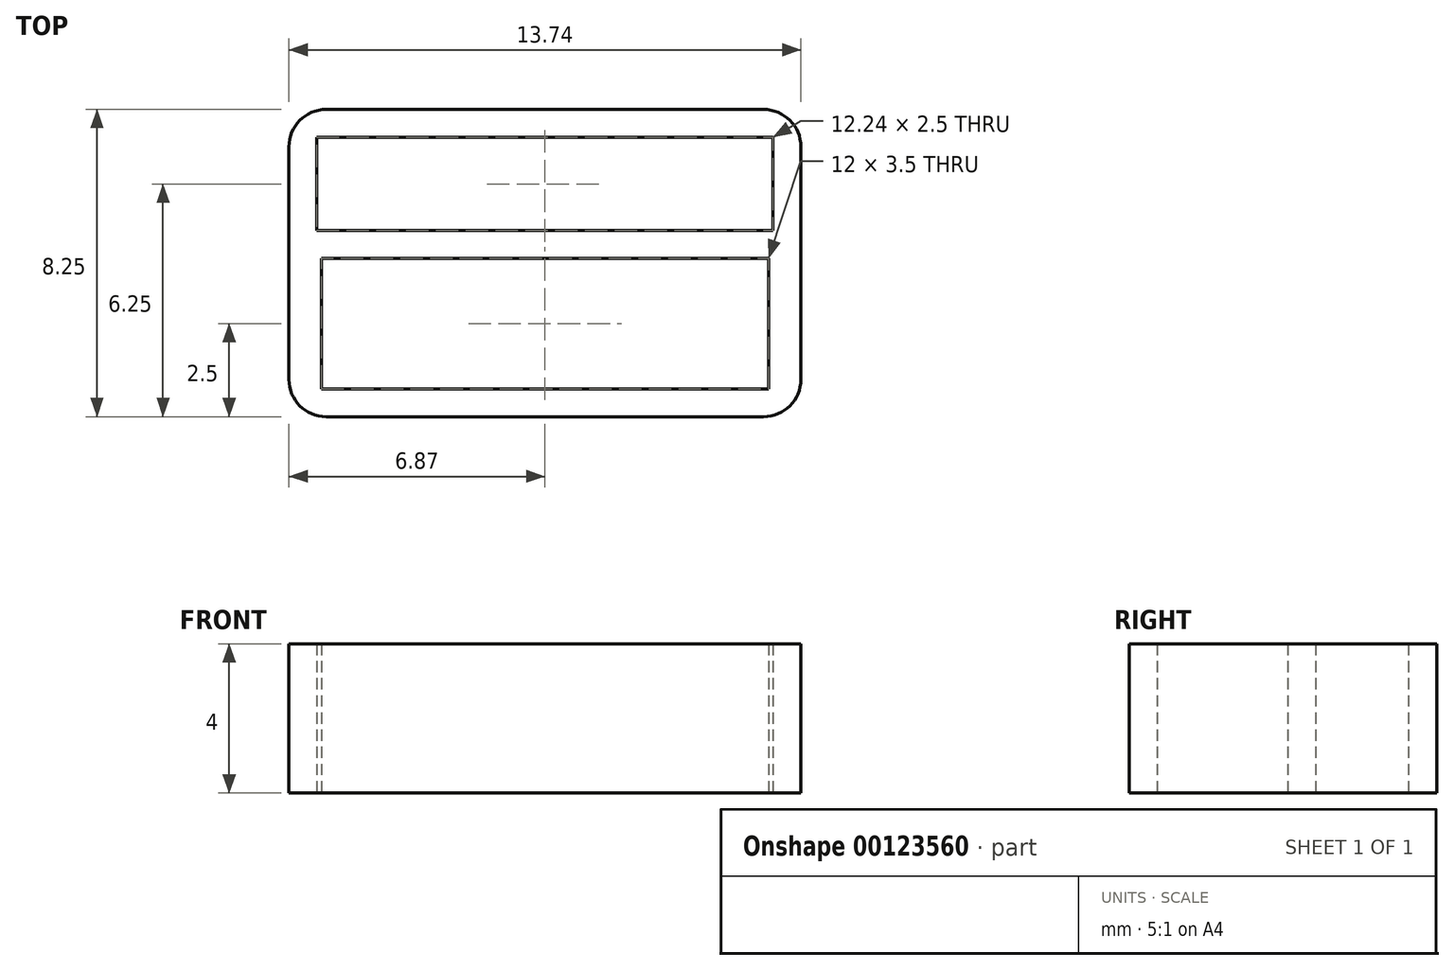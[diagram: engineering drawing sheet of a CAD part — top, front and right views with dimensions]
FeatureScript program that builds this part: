
annotation { "Feature Type Name" : "Feature", "Feature Type Description" : "" }
export const myFeature = defineFeature(function(context is Context, id is Id, definition is map)
    precondition{}
    {
        {
            var Q0;
            Q0=qCreatedBy(makeId("Top.planeOp"),FACE);
            var sketch = newSketch(context, id + "F0", { "sketchPlane" : qUnion([Q0])});
            skLineSegment(sketch, "E0.bottom", {"start": v(0, 0) * mm, "end": v(13.74, 0) * mm});
            skLineSegment(sketch, "E0.top", {"start": v(0, 8.25) * mm, "end": v(13.74, 8.25) * mm});
            skLineSegment(sketch, "E0.left", {"start": v(0, 0) * mm, "end": v(0, 8.25) * mm});
            skLineSegment(sketch, "E0.right", {"start": v(13.74, 0) * mm, "end": v(13.74, 8.25) * mm});
            skLineSegment(sketch, "E1.bottom", {"start": v(0.75, 7.5) * mm, "end": v(13, 7.5) * mm});
            skLineSegment(sketch, "E1.top", {"start": v(0.75, 5) * mm, "end": v(13, 5) * mm});
            skLineSegment(sketch, "E1.left", {"start": v(0.75, 7.5) * mm, "end": v(0.75, 5) * mm});
            skLineSegment(sketch, "E1.right", {"start": v(13, 7.5) * mm, "end": v(13, 5) * mm});
            skLineSegment(sketch, "E2.bottom", {"start": v(0.87, 4.25) * mm, "end": v(12.87, 4.25) * mm});
            skLineSegment(sketch, "E2.top", {"start": v(0.87, 0.75) * mm, "end": v(12.87, 0.75) * mm});
            skLineSegment(sketch, "E2.left", {"start": v(0.87, 4.25) * mm, "end": v(0.87, 0.75) * mm});
            skLineSegment(sketch, "E2.right", {"start": v(12.87, 4.25) * mm, "end": v(12.87, 0.75) * mm});
            skSolve(sketch);
        }
        {
            var Q0;
            Q0 = qSketchRegion(id + "F0", true);
            extrude(context, id + "F1", {"entities" : qUnion([Q0]), "depth" : 4 * mm});
        }
        {
            var Q0;
            Q0=makeQuery(id+"F1.opExtrude","SWEPT_EDGE",EDGE,{"disambiguationData":[OSD([sQuery(id+"F0.wireOp",EDGE,"E0.bottom"),sQuery(id+"F0.wireOp",EDGE,"E0.left")])]});
            var Q1;
            Q1=makeQuery(id+"F1.opExtrude","SWEPT_EDGE",EDGE,{"disambiguationData":[OSD([sQuery(id+"F0.wireOp",EDGE,"E0.bottom"),sQuery(id+"F0.wireOp",EDGE,"E0.right")])]});
            var Q2;
            Q2=makeQuery(id+"F1.opExtrude","SWEPT_EDGE",EDGE,{"disambiguationData":[OSD([sQuery(id+"F0.wireOp",EDGE,"E0.top"),sQuery(id+"F0.wireOp",EDGE,"E0.right")])]});
            var Q3;
            Q3=makeQuery(id+"F1.opExtrude","SWEPT_EDGE",EDGE,{"disambiguationData":[OSD([sQuery(id+"F0.wireOp",EDGE,"E0.top"),sQuery(id+"F0.wireOp",EDGE,"E0.left")])]});
            fillet(context, id + "F2", {"entities" : qUnion([Q0, Q1, Q2, Q3]), "radius" : 1 * mm, "tangentPropagation" : true, "allowEdgeOverflow" : false});
        }
    });
